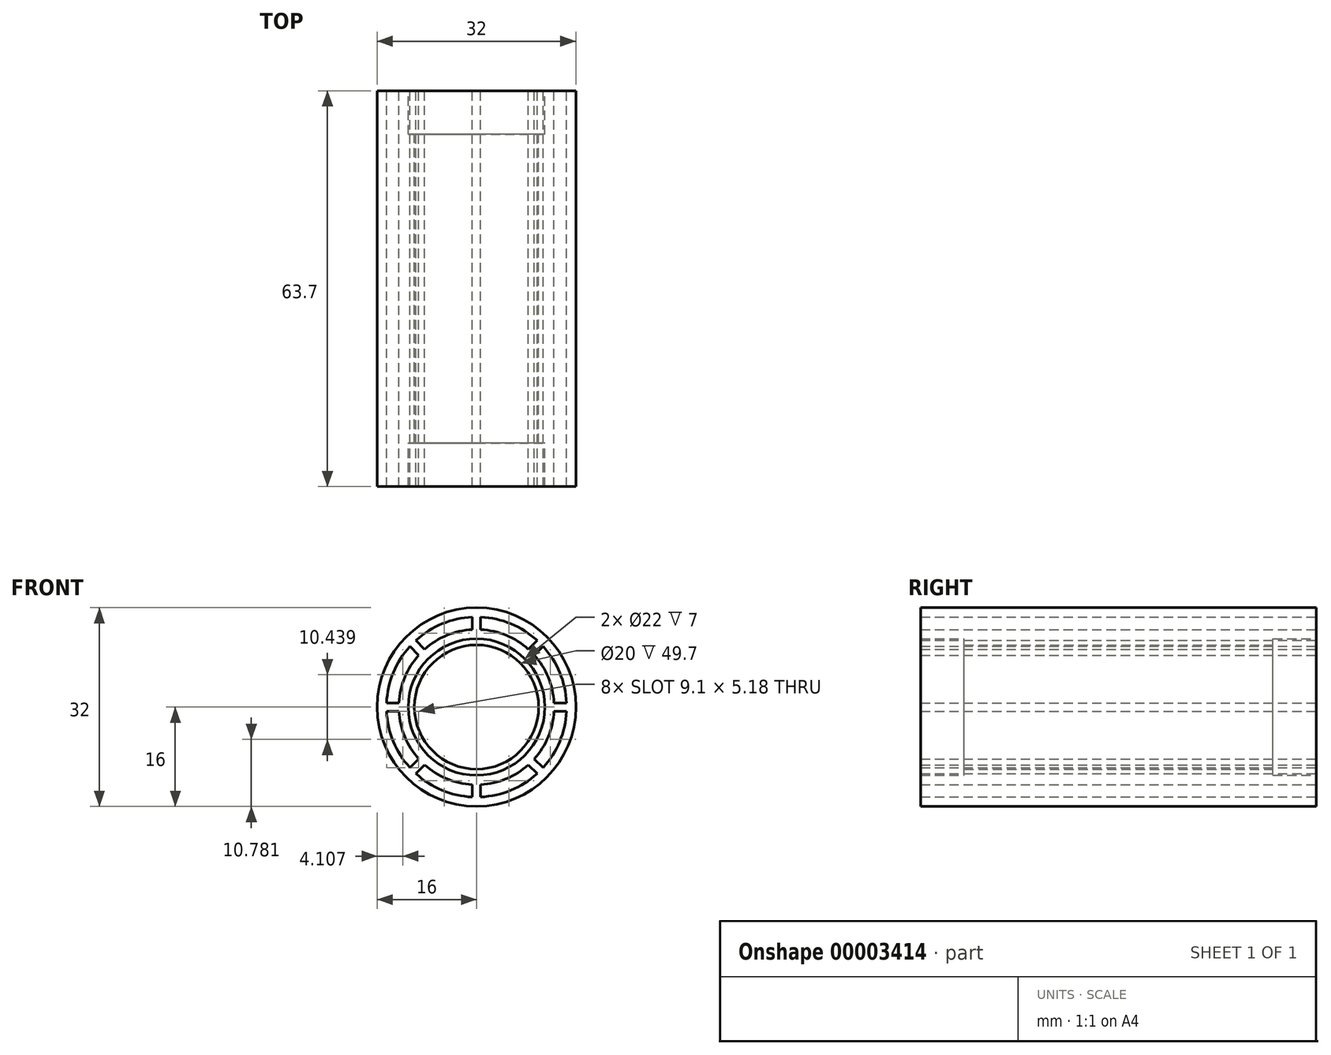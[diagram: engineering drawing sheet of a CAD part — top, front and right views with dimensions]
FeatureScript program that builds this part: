
annotation { "Feature Type Name" : "Feature", "Feature Type Description" : "" }
export const myFeature = defineFeature(function(context is Context, id is Id, definition is map)
    precondition{}
    {
        {
            var Q0;
            Q0=qCreatedBy(makeId("Front.planeOp"),FACE);
            var sketch = newSketch(context, id + "F0", { "sketchPlane" : qUnion([Q0])});
            skCircle(sketch, "E0", {"center": v(0, 0) * mm, "radius": 16 * mm});
            skCircle(sketch, "E1", {"center": v(0, 0) * mm, "radius": 11 * mm});
            skCircle(sketch, "E2", {"center": v(0, 0) * mm, "radius": 14.5 * mm});
            skCircle(sketch, "E3", {"center": v(0, 0) * mm, "radius": 12.5 * mm});
            skLineSegment(sketch, "E4", {"start": v(-0.67, 14.48) * mm, "end": v(-0.67, 12.48) * mm});
            skLineSegment(sketch, "E5", {"start": v(0, 0) * mm, "end": v(0, 17.1) * mm, "construction": true});
            skLineSegment(sketch, "E6.0.MirrorCS", {"start": v(0.67, 14.48) * mm, "end": v(0.67, 12.48) * mm});
            skSolve(sketch);
        }
        {
            var Q0;
            Q0=makeQuery(id+"F0.imprint","IMPRINT",FACE,{"disambiguationData":[TD([[makeQuery(id+"F0.imprint","IMPRINT",EDGE,{"derivedFrom":sQuery(id+"F0.wireOp",EDGE,"E0")}),1.0]])]});
            var Q1;
            Q1=makeQuery(id+"F0.imprint","IMPRINT",FACE,{"disambiguationData":[TD([[makeQuery(id+"F0.imprint","IMPRINT",EDGE,{"derivedFrom":sQuery(id+"F0.wireOp",EDGE,"E1")}),-1.0]])]});
            extrude(context, id + "F1", {"entities" : qUnion([Q0, Q1]), "depth" : 63.7 * mm});
        }
        {
            var Q0;
            {var subQ1=sQuery(id+"F0.wireOp",EDGE,"E4");Q0=makeQuery(id+"F0.imprint","IMPRINT",FACE,{"disambiguationData":[TD([[makeQuery(id+"F0.imprint","IMPRINT",EDGE,{"derivedFrom":subQ1}),1.0]])]});}
            extrude(context, id + "F2", {"entities" : qUnion([Q0]), "depth" : 63.7 * mm});
        }
        {
            var Q0;
            Q0=makeQuery(id+"F2.opExtrude","SWEPT_BODY",BODY,{"disambiguationData":[OSD([sQuery(id+"F0.wireOp",EDGE,"E2"),sQuery(id+"F0.wireOp",EDGE,"E3"),sQuery(id+"F0.wireOp",EDGE,"E4"),sQuery(id+"F0.wireOp",EDGE,"E6.0.MirrorCS")])]});
            var Q1;
            Q1=makeQuery(id+"F1.opExtrude","SWEPT_FACE",FACE,{"disambiguationData":[OSD([sQuery(id+"F0.wireOp",EDGE,"E2")])]});
            circularPattern(context, id + "F3", {"entities" : qUnion([Q0]), "axis" : qUnion([Q1]), "angle" : 360 * degree, "instanceCount" : 8, "equalSpace" : true});
        }
        {
            var Q0;
            Q0=makeQuery(id+"F1.opExtrude","SWEPT_BODY",BODY,{"disambiguationData":[OSD([sQuery(id+"F0.wireOp",EDGE,"E0"),sQuery(id+"F0.wireOp",EDGE,"E2")])]});
            var Q1;
            Q1=makeQuery(id+"F1.opExtrude","SWEPT_BODY",BODY,{"disambiguationData":[OSD([sQuery(id+"F0.wireOp",EDGE,"E1"),sQuery(id+"F0.wireOp",EDGE,"E3")])]});
            var Q2;
            Q2=makeQuery(id+"F2.opExtrude","SWEPT_BODY",BODY,{"disambiguationData":[OSD([sQuery(id+"F0.wireOp",EDGE,"E2"),sQuery(id+"F0.wireOp",EDGE,"E3"),sQuery(id+"F0.wireOp",EDGE,"E4"),sQuery(id+"F0.wireOp",EDGE,"E6.0.MirrorCS")])]});
            var Q3;
            Q3=makeQuery(id+"F3.opPattern","COPY",BODY,{"derivedFrom":makeQuery(id+"F2.opExtrude","SWEPT_BODY",BODY,{"disambiguationData":[OSD([sQuery(id+"F0.wireOp",EDGE,"E2"),sQuery(id+"F0.wireOp",EDGE,"E3"),sQuery(id+"F0.wireOp",EDGE,"E4"),sQuery(id+"F0.wireOp",EDGE,"E6.0.MirrorCS")])]}),"instanceName":"1"});
            var Q4;
            Q4=makeQuery(id+"F3.opPattern","COPY",BODY,{"derivedFrom":makeQuery(id+"F2.opExtrude","SWEPT_BODY",BODY,{"disambiguationData":[OSD([sQuery(id+"F0.wireOp",EDGE,"E2"),sQuery(id+"F0.wireOp",EDGE,"E3"),sQuery(id+"F0.wireOp",EDGE,"E4"),sQuery(id+"F0.wireOp",EDGE,"E6.0.MirrorCS")])]}),"instanceName":"2"});
            var Q5;
            Q5=makeQuery(id+"F3.opPattern","COPY",BODY,{"derivedFrom":makeQuery(id+"F2.opExtrude","SWEPT_BODY",BODY,{"disambiguationData":[OSD([sQuery(id+"F0.wireOp",EDGE,"E2"),sQuery(id+"F0.wireOp",EDGE,"E3"),sQuery(id+"F0.wireOp",EDGE,"E4"),sQuery(id+"F0.wireOp",EDGE,"E6.0.MirrorCS")])]}),"instanceName":"3"});
            var Q6;
            Q6=makeQuery(id+"F3.opPattern","COPY",BODY,{"derivedFrom":makeQuery(id+"F2.opExtrude","SWEPT_BODY",BODY,{"disambiguationData":[OSD([sQuery(id+"F0.wireOp",EDGE,"E2"),sQuery(id+"F0.wireOp",EDGE,"E3"),sQuery(id+"F0.wireOp",EDGE,"E4"),sQuery(id+"F0.wireOp",EDGE,"E6.0.MirrorCS")])]}),"instanceName":"4"});
            var Q7;
            Q7=makeQuery(id+"F3.opPattern","COPY",BODY,{"derivedFrom":makeQuery(id+"F2.opExtrude","SWEPT_BODY",BODY,{"disambiguationData":[OSD([sQuery(id+"F0.wireOp",EDGE,"E2"),sQuery(id+"F0.wireOp",EDGE,"E3"),sQuery(id+"F0.wireOp",EDGE,"E4"),sQuery(id+"F0.wireOp",EDGE,"E6.0.MirrorCS")])]}),"instanceName":"5"});
            var Q8;
            Q8=makeQuery(id+"F3.opPattern","COPY",BODY,{"derivedFrom":makeQuery(id+"F2.opExtrude","SWEPT_BODY",BODY,{"disambiguationData":[OSD([sQuery(id+"F0.wireOp",EDGE,"E2"),sQuery(id+"F0.wireOp",EDGE,"E3"),sQuery(id+"F0.wireOp",EDGE,"E4"),sQuery(id+"F0.wireOp",EDGE,"E6.0.MirrorCS")])]}),"instanceName":"6"});
            var Q9;
            Q9=makeQuery(id+"F3.opPattern","COPY",BODY,{"derivedFrom":makeQuery(id+"F2.opExtrude","SWEPT_BODY",BODY,{"disambiguationData":[OSD([sQuery(id+"F0.wireOp",EDGE,"E2"),sQuery(id+"F0.wireOp",EDGE,"E3"),sQuery(id+"F0.wireOp",EDGE,"E4"),sQuery(id+"F0.wireOp",EDGE,"E6.0.MirrorCS")])]}),"instanceName":"7"});
            var Q10;
            Q10=makeQuery(id+"F3.opPattern","COPY",BODY,{"derivedFrom":makeQuery(id+"F2.opExtrude","SWEPT_BODY",BODY,{"disambiguationData":[OSD([sQuery(id+"F0.wireOp",EDGE,"E2"),sQuery(id+"F0.wireOp",EDGE,"E3"),sQuery(id+"F0.wireOp",EDGE,"E4"),sQuery(id+"F0.wireOp",EDGE,"E6.0.MirrorCS")])]}),"instanceName":"8"});
            var Q11;
            Q11=makeQuery(id+"F3.opPattern","COPY",BODY,{"derivedFrom":makeQuery(id+"F2.opExtrude","SWEPT_BODY",BODY,{"disambiguationData":[OSD([sQuery(id+"F0.wireOp",EDGE,"E2"),sQuery(id+"F0.wireOp",EDGE,"E3"),sQuery(id+"F0.wireOp",EDGE,"E4"),sQuery(id+"F0.wireOp",EDGE,"E6.0.MirrorCS")])]}),"instanceName":"9"});
            var Q12;
            Q12=makeQuery(id+"F3.opPattern","COPY",BODY,{"derivedFrom":makeQuery(id+"F2.opExtrude","SWEPT_BODY",BODY,{"disambiguationData":[OSD([sQuery(id+"F0.wireOp",EDGE,"E2"),sQuery(id+"F0.wireOp",EDGE,"E3"),sQuery(id+"F0.wireOp",EDGE,"E4"),sQuery(id+"F0.wireOp",EDGE,"E6.0.MirrorCS")])]}),"instanceName":"10"});
            var Q13;
            Q13=makeQuery(id+"F3.opPattern","COPY",BODY,{"derivedFrom":makeQuery(id+"F2.opExtrude","SWEPT_BODY",BODY,{"disambiguationData":[OSD([sQuery(id+"F0.wireOp",EDGE,"E2"),sQuery(id+"F0.wireOp",EDGE,"E3"),sQuery(id+"F0.wireOp",EDGE,"E4"),sQuery(id+"F0.wireOp",EDGE,"E6.0.MirrorCS")])]}),"instanceName":"11"});
            booleanBodies(context, id + "F4", {"operationType" : BooleanOperationType.UNION, "tools" : qUnion([Q0, Q1, Q2, Q3, Q4, Q5, Q6, Q7, Q8, Q9, Q10, Q11, Q12, Q13])});
        }
        {
            var Q0;
            {var subQ0=sQuery(id+"F0.wireOp",EDGE,"E2");var subQ1=sQuery(id+"F0.wireOp",EDGE,"E3");var subQ2=makeQuery(id+"F2.opExtrude","CAP_FACE",FACE,{"disambiguationData":[OSD([subQ0,subQ1,sQuery(id+"F0.wireOp",EDGE,"E4"),sQuery(id+"F0.wireOp",EDGE,"E6.0.MirrorCS")])],"isStart":false});Q0=makeQuery(id+"F4.opBoolean","MERGE",FACE,{"derivedFrom":[makeQuery(id+"F1.opExtrude","CAP_FACE",FACE,{"disambiguationData":[OSD([sQuery(id+"F0.wireOp",EDGE,"E0"),subQ0])],"isStart":false}),makeQuery(id+"F1.opExtrude","CAP_FACE",FACE,{"disambiguationData":[OSD([sQuery(id+"F0.wireOp",EDGE,"E1"),subQ1])],"isStart":false}),subQ2,makeQuery(id+"F3.opPattern","COPY",FACE,{"derivedFrom":subQ2,"instanceName":"1"}),makeQuery(id+"F3.opPattern","COPY",FACE,{"derivedFrom":subQ2,"instanceName":"2"}),makeQuery(id+"F3.opPattern","COPY",FACE,{"derivedFrom":subQ2,"instanceName":"3"}),makeQuery(id+"F3.opPattern","COPY",FACE,{"derivedFrom":subQ2,"instanceName":"4"}),makeQuery(id+"F3.opPattern","COPY",FACE,{"derivedFrom":subQ2,"instanceName":"5"}),makeQuery(id+"F3.opPattern","COPY",FACE,{"derivedFrom":subQ2,"instanceName":"6"}),makeQuery(id+"F3.opPattern","COPY",FACE,{"derivedFrom":subQ2,"instanceName":"7"})]});}
            cPlane(context, id + "F5", {"entities" : qUnion([Q0]), "cplaneType" : CPlaneType.OFFSET, "offset" : 7 * mm, "oppositeDirection" : true, "width" : 150 * mm, "height" : 150 * mm});
        }
        {
            var Q0;
            Q0=makeQuery(id+"F0.imprint","IMPRINT",FACE,{"disambiguationData":[TD([[makeQuery(id+"F0.imprint","IMPRINT",EDGE,{"derivedFrom":sQuery(id+"F0.wireOp",EDGE,"E0")}),1.0]])]});
            cPlane(context, id + "F6", {"entities" : qUnion([Q0]), "cplaneType" : CPlaneType.OFFSET, "offset" : 7 * mm, "width" : 150 * mm, "height" : 150 * mm});
        }
        {
            var Q0;
            Q0=qCreatedBy(id+"F6.planeOp",FACE);
            var sketch = newSketch(context, id + "F7", { "sketchPlane" : qUnion([Q0])});
            skCircle(sketch, "E7", {"center": v(0, 0) * mm, "radius": 10 * mm});
            skCircle(sketch, "E8", {"center": v(0, 0) * mm, "radius": 11 * mm});
            skSolve(sketch);
        }
        {
            var Q0;
            Q0=makeQuery(id+"F7.imprint","IMPRINT",FACE,{"disambiguationData":[TD([[makeQuery(id+"F7.imprint","IMPRINT",EDGE,{"derivedFrom":sQuery(id+"F7.wireOp",EDGE,"E7")}),-1.0]])]});
            var Q1;
            Q1=sQuery(id+"F7.wireOp",EDGE,"E7");
            var Q2;
            Q2=qCreatedBy(id+"F5.planeOp",FACE);
            extrude(context, id + "F8", {"entities" : qUnion([Q0]), "operationType" : NewBodyOperationType.ADD, "surfaceEntities" : qUnion([Q1]), "endBound" : BoundingType.UP_TO_SURFACE, "endBoundEntityFace" : qUnion([Q2]), "depth" : 25 * mm});
        }
    });
